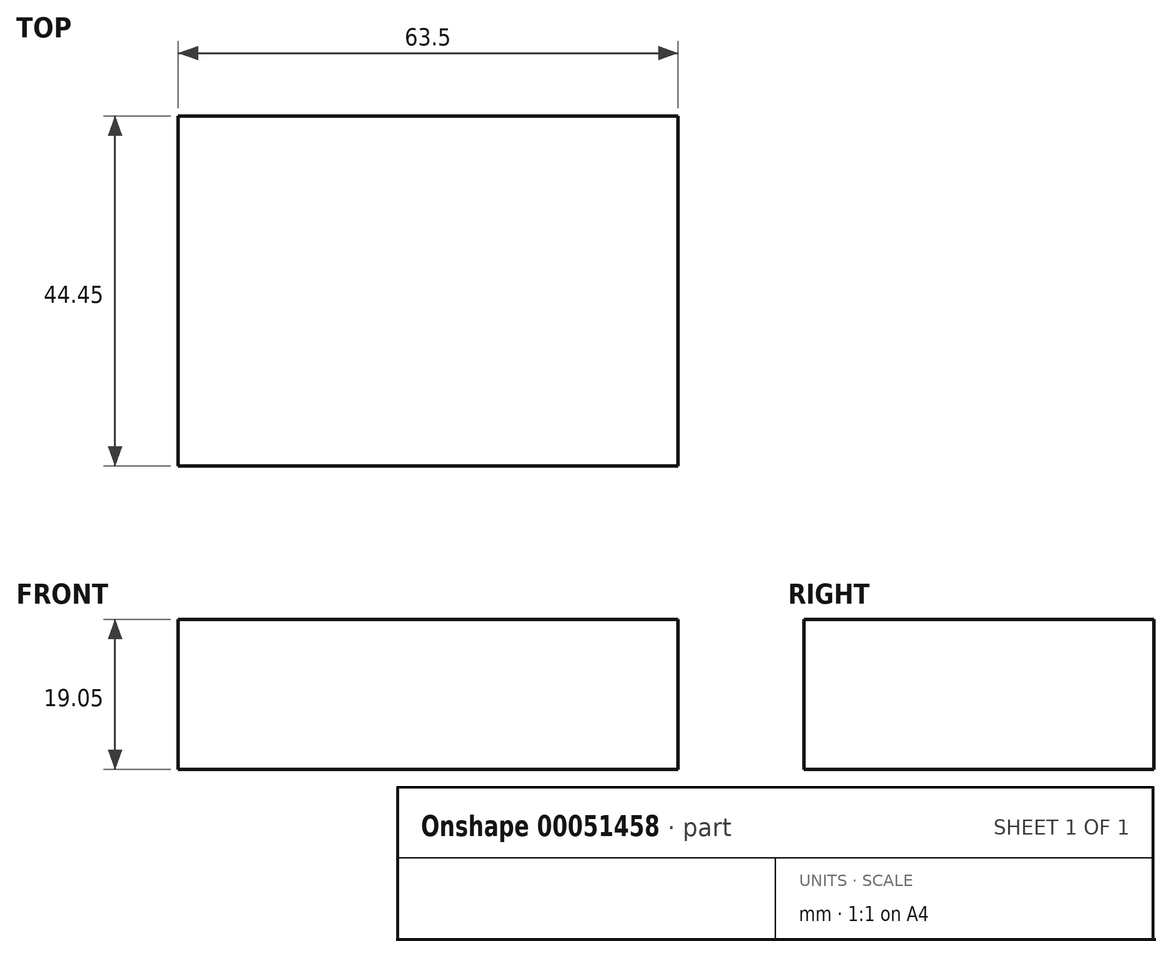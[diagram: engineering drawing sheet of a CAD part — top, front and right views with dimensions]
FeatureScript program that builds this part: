
annotation { "Feature Type Name" : "Feature", "Feature Type Description" : "" }
export const myFeature = defineFeature(function(context is Context, id is Id, definition is map)
    precondition{}
    {
        {
            var Q0;
            Q0=qCreatedBy(makeId("Front.planeOp"),FACE);
            var sketch = newSketch(context, id + "F0", { "sketchPlane" : qUnion([Q0])});
            skLineSegment(sketch, "E0.bottom", {"start": v(-51.7, 36.24) * mm, "end": v(11.8, 36.24) * mm});
            skLineSegment(sketch, "E0.top", {"start": v(-51.7, 17.2) * mm, "end": v(11.8, 17.2) * mm});
            skLineSegment(sketch, "E0.left", {"start": v(-51.7, 36.24) * mm, "end": v(-51.7, 17.2) * mm});
            skLineSegment(sketch, "E0.right", {"start": v(11.8, 36.24) * mm, "end": v(11.8, 17.2) * mm});
            skSolve(sketch);
        }
        {
            var Q0;
            Q0 = qSketchRegion(id + "F0", true);
            extrude(context, id + "F1", {"entities" : qUnion([Q0]), "depth" : 44.45 * mm});
        }
    });
